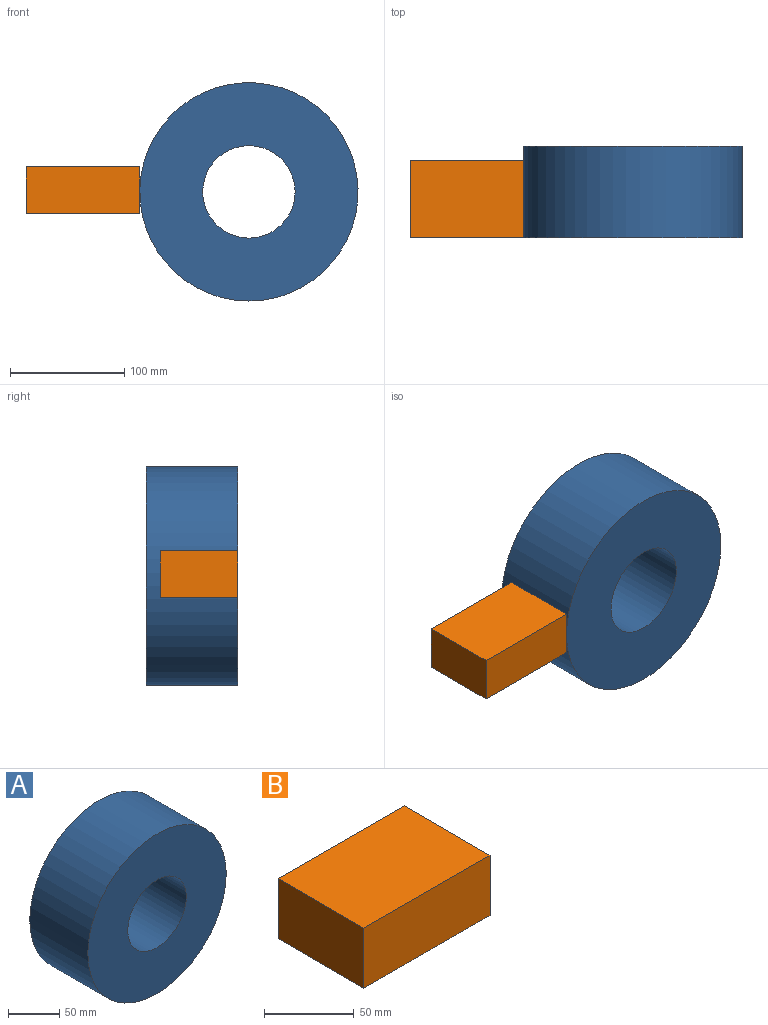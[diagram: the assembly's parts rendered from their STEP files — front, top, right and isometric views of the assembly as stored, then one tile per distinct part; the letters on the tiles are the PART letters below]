
ASSEMBLY  parts=2 mates=1
PART A: 4 faces, bbox 190.7x80x190.7 mm
  f0: cylinder r=40.35mm len=80.7mm, axis (0,-1,0), area 20282.7mm2, adj f2,f3
  f1: cylinder r=95.35mm len=190.7mm, axis (0,-1,0), area 47928.7mm2, adj f2,f3
  f2: plane 190.7x190.7mm, normal (0,1,0), area 23447.7mm2, adj f0,f1
  f3: plane 190.7x190.7mm, normal (0,-1,0), area 23447.7mm2, adj f0,f1
PART B: 6 faces, bbox 99.4x67.8x41 mm
  f0: plane 67.83x41mm, normal (-1,0,0), area 2781.1mm2, adj f1,f3,f4,f5
  f1: plane 99.44x41mm, normal (0,-1,0), area 4076.9mm2, adj f0,f2,f4,f5
  f2: plane 67.83x41mm, normal (1,0,0), area 2781.1mm2, adj f1,f3,f4,f5
  f3: plane 99.44x41mm, normal (0,1,0), area 4076.9mm2, adj f0,f2,f4,f5
  f4: plane 99.44x67.83mm, normal (0,0,1), area 6745mm2, adj f0,f1,f2,f3
  f5: plane 99.44x67.83mm, normal (0,0,-1), area 6745mm2, adj f0,f1,f2,f3
PLACE A t=(165.25,-16.62,19.05)mm
PLACE B t=(20.32,3.83,0)mm
MATE planar A.f1 <-> B.f1  axis (0,-1,0) through (165.25,-16.62,19.05)mm
